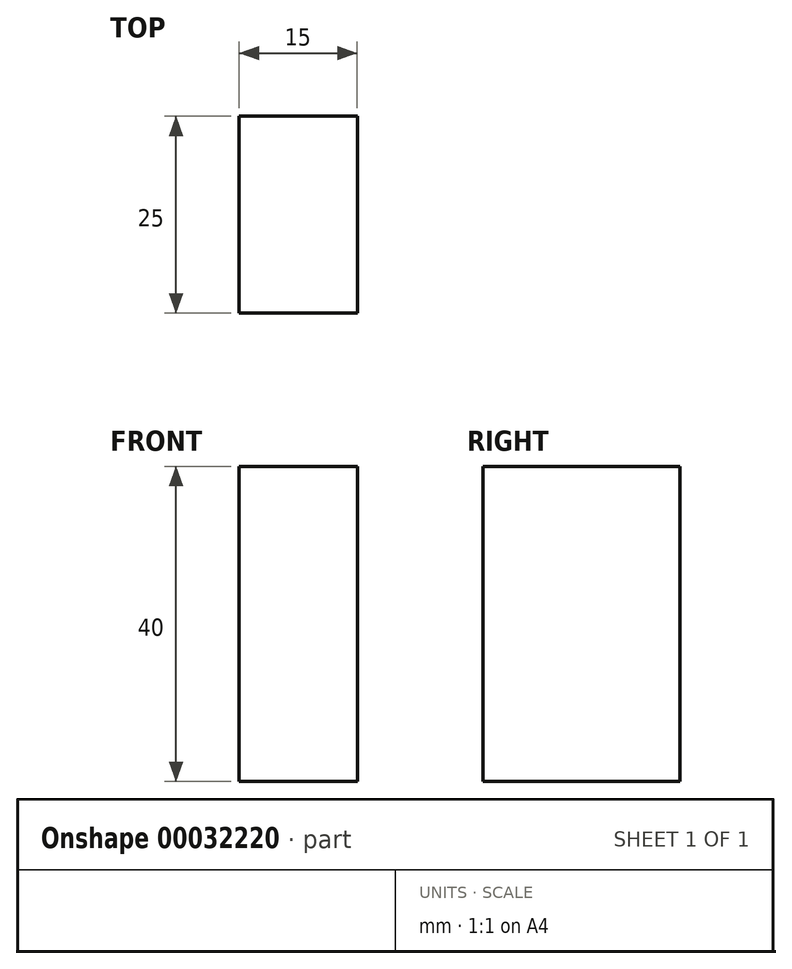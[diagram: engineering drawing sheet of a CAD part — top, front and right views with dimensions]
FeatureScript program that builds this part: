
annotation { "Feature Type Name" : "Feature", "Feature Type Description" : "" }
export const myFeature = defineFeature(function(context is Context, id is Id, definition is map)
    precondition{}
    {
        {
            var Q0;
            Q0=qCreatedBy(makeId("Front.planeOp"),FACE);
            var sketch = newSketch(context, id + "F0", { "sketchPlane" : qUnion([Q0])});
            skLineSegment(sketch, "E0.bottom", {"start": v(-20.4, 36.73) * mm, "end": v(-5.4, 36.73) * mm});
            skLineSegment(sketch, "E0.top", {"start": v(-20.4, -3.27) * mm, "end": v(-5.4, -3.27) * mm});
            skLineSegment(sketch, "E0.left", {"start": v(-20.4, 36.73) * mm, "end": v(-20.4, -3.27) * mm});
            skLineSegment(sketch, "E0.right", {"start": v(-5.4, 36.73) * mm, "end": v(-5.4, -3.27) * mm});
            skSolve(sketch);
        }
        {
            var Q0;
            Q0 = qSketchRegion(id + "F0", true);
            extrude(context, id + "F1", {"entities" : qUnion([Q0]), "depth" : 25 * mm});
        }
    });
